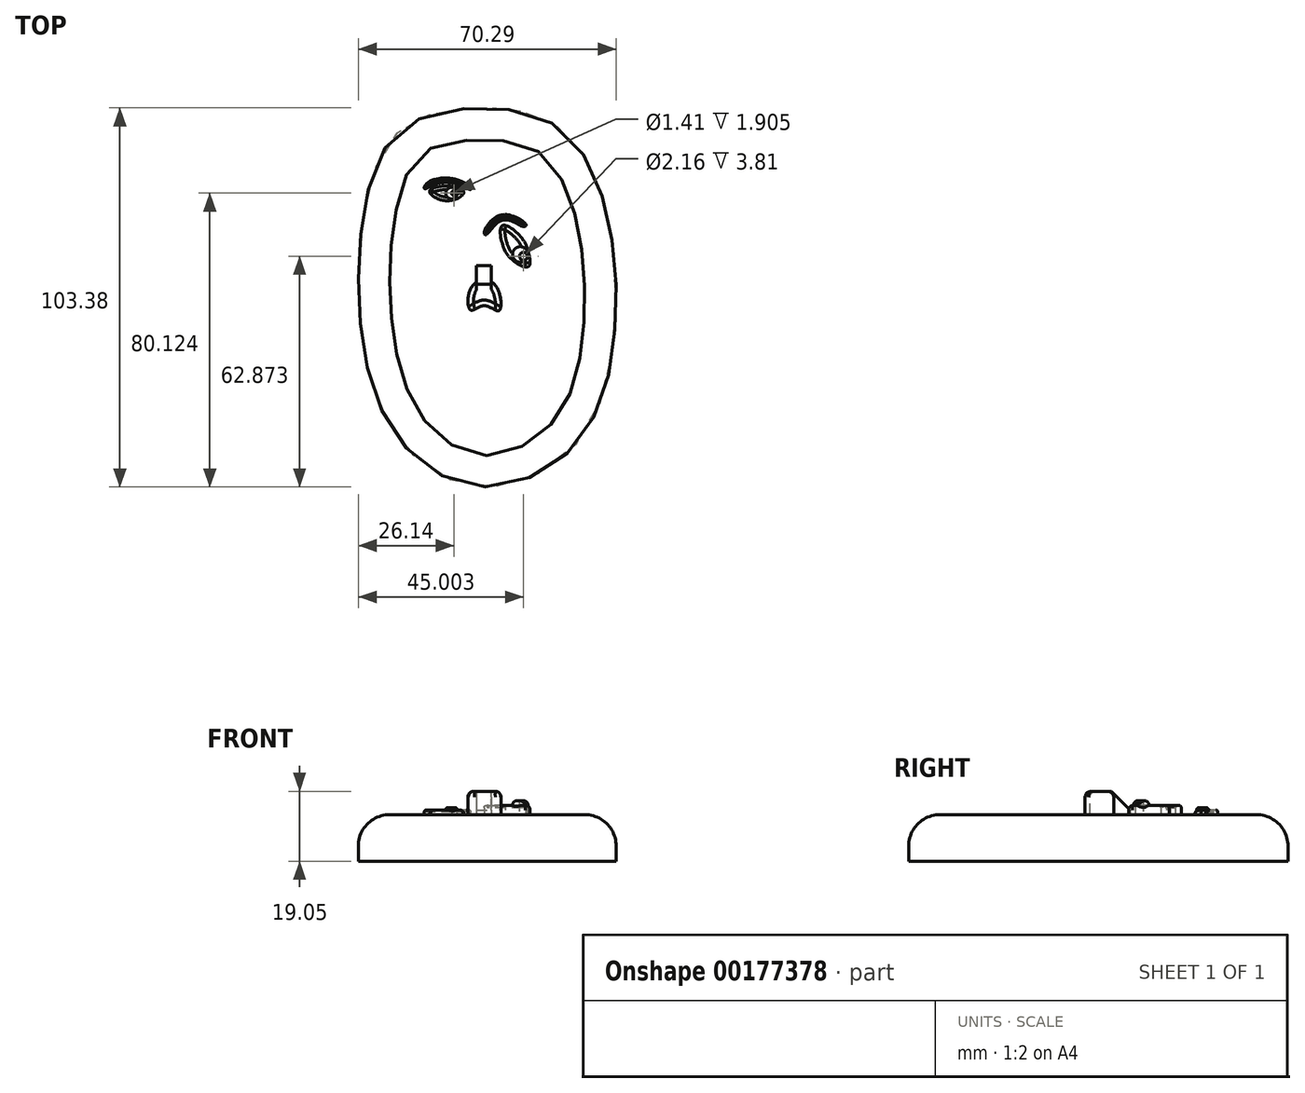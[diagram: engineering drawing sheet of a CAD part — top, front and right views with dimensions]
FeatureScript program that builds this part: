
annotation { "Feature Type Name" : "Feature", "Feature Type Description" : "" }
export const myFeature = defineFeature(function(context is Context, id is Id, definition is map)
    precondition{}
    {
        {
            var Q0;
            Q0=qCreatedBy(makeId("Top.planeOp"),FACE);
            var sketch = newSketch(context, id + "F0", { "sketchPlane" : qUnion([Q0])});
            skFitSpline(sketch, "E0", {"points": [v(-5.64, 49.3) * mm, v(-21.96, 44.26) * mm, v(-32.02, 25.34) * mm, v(-33.58, -10.93) * mm, v(-22.82, -41.3) * mm, v(0, -53.8) * mm, v(25.08, -42) * mm, v(35.5, -12.32) * mm, v(32.2, 25.34) * mm, v(19.53, 44.78) * mm, v(4.95, 49.3) * mm, v(-5.64, 49.3) * mm]});
            skSolve(sketch);
        }
        {
            var Q0;
            Q0=makeQuery(id+"F0.imprint","IMPRINT",FACE,{"disambiguationData":[TD([[makeQuery(id+"F0.imprint","IMPRINT",EDGE,{"derivedFrom":sQuery(id+"F0.wireOp",EDGE,"E0")}),1.0]])]});
            extrude(context, id + "F1", {"entities" : qUnion([Q0]), "depth" : 12.7 * mm});
        }
        {
            var Q0;
            Q0=makeQuery(id+"F1.opExtrude","CAP_EDGE",EDGE,{"disambiguationData":[OSD([sQuery(id+"F0.wireOp",EDGE,"E0")])],"isStart":false});
            fillet(context, id + "F2", {"entities" : qUnion([Q0]), "radius" : 8.58 * mm, "tangentPropagation" : true, "allowEdgeOverflow" : false});
        }
        {
            var Q0;
            Q0=makeQuery(id+"F1.opExtrude","CAP_FACE",FACE,{"disambiguationData":[OSD([sQuery(id+"F0.wireOp",EDGE,"E0")])],"isStart":false});
            var sketch = newSketch(context, id + "F3", { "sketchPlane" : qUnion([Q0])});
            skFitSpline(sketch, "E1", {"points": [v(-14.92, 26.83) * mm, v(-12.77, 28) * mm, v(-8.2, 28.03) * mm, v(-5.58, 26.54) * mm, v(-8.03, 24.57) * mm, v(-12.73, 24.79) * mm, v(-14.92, 26.83) * mm]});
            skCircle(sketch, "E2", {"center": v(-8.94, 26.28) * mm, "radius": 1.57 * mm});
            skCircle(sketch, "E3", {"center": v(-8.94, 26.28) * mm, "radius": 0.84 * mm});
            skSolve(sketch);
        }
        {
            var Q0;
            Q0=makeQuery(id+"F3.imprint","IMPRINT",FACE,{"disambiguationData":[TD([[makeQuery(id+"F3.imprint","IMPRINT",EDGE,{"derivedFrom":sQuery(id+"F3.wireOp",EDGE,"E1")}),-1.0]])]});
            extrude(context, id + "F4", {"entities" : qUnion([Q0]), "operationType" : NewBodyOperationType.ADD, "depth" : 1.27 * mm});
        }
        {
            var Q0;
            Q0=makeQuery(id+"F4.boolean.opBoolean","SPLIT",FACE,{"disambiguationData":[TD([makeQuery(id+"F4.opExtrude","SWEPT_FACE",FACE,{"disambiguationData":[OSD([sQuery(id+"F3.wireOp",EDGE,"E2")])]})])],"derivedFrom":makeQuery(id+"F1.opExtrude","CAP_FACE",FACE,{"disambiguationData":[OSD([sQuery(id+"F0.wireOp",EDGE,"E0")])],"isStart":false})});
            var sketch = newSketch(context, id + "F5", { "sketchPlane" : qUnion([Q0])});
            skCircle(sketch, "E4", {"center": v(-8.21, 26.31) * mm, "radius": 0.7 * mm});
            skCircle(sketch, "E5", {"center": v(-8.21, 26.31) * mm, "radius": 0.3 * mm});
            skSolve(sketch);
        }
        {
            var Q0;
            Q0=makeQuery(id+"F5.imprint","IMPRINT",FACE,{"disambiguationData":[TD([[makeQuery(id+"F5.imprint","IMPRINT",EDGE,{"derivedFrom":sQuery(id+"F5.wireOp",EDGE,"E4")}),-1.0]])]});
            extrude(context, id + "F6", {"entities" : qUnion([Q0]), "operationType" : NewBodyOperationType.ADD, "depth" : 1.9 * mm});
        }
        {
            var Q0;
            Q0=makeQuery(id+"F4.opExtrude","CAP_EDGE",EDGE,{"disambiguationData":[OSD([sQuery(id+"F3.wireOp",EDGE,"E1")])],"isStart":false});
            fillet(context, id + "F7", {"entities" : qUnion([Q0]), "radius" : 1.02 * mm, "tangentPropagation" : true, "allowEdgeOverflow" : false});
        }
        {
            var Q0;
            Q0=makeQuery(id+"F6.opExtrude","CAP_EDGE",EDGE,{"disambiguationData":[OSD([sQuery(id+"F3.wireOp",EDGE,"E2")])],"isStart":false});
            fillet(context, id + "F8", {"entities" : qUnion([Q0]), "radius" : 0.5 * mm, "tangentPropagation" : true, "allowEdgeOverflow" : false});
        }
        {
            var Q0;
            {var subQ0=sQuery(id+"F0.wireOp",EDGE,"E0");Q0=makeQuery(id+"F4.boolean.opBoolean","SPLIT",FACE,{"disambiguationData":[TD([makeQuery(id+"F2.opFillet","BLEND_FACE",FACE,{"disambiguationData":[OSD([subQ0])]})])],"derivedFrom":makeQuery(id+"F1.opExtrude","CAP_FACE",FACE,{"disambiguationData":[OSD([subQ0])],"isStart":false})});}
            var sketch = newSketch(context, id + "F9", { "sketchPlane" : qUnion([Q0])});
            skFitSpline(sketch, "E6", {"points": [v(-15.7, 27.64) * mm, v(-10.41, 29.23) * mm, v(-4.31, 27.4) * mm, v(-3.73, 27.32) * mm, v(-3.75, 27.86) * mm, v(-6.87, 29.75) * mm, v(-10.24, 30.4) * mm, v(-14.3, 29.81) * mm, v(-16.27, 28.14) * mm, v(-16.27, 27.47) * mm, v(-15.7, 27.64) * mm]});
            skSolve(sketch);
        }
        {
            var Q0;
            Q0=makeQuery(id+"F9.imprint","IMPRINT",FACE,{"disambiguationData":[TD([[makeQuery(id+"F9.imprint","IMPRINT",EDGE,{"derivedFrom":sQuery(id+"F9.wireOp",EDGE,"E6")}),1.0]])]});
            extrude(context, id + "F10", {"entities" : qUnion([Q0]), "operationType" : NewBodyOperationType.ADD, "depth" : 1.27 * mm});
        }
        {
            var Q0;
            Q0=makeQuery(id+"F10.opExtrude","CAP_EDGE",EDGE,{"disambiguationData":[OSD([sQuery(id+"F9.wireOp",EDGE,"E6")])],"isStart":false});
            fillet(context, id + "F11", {"entities" : qUnion([Q0]), "radius" : 0.5 * mm, "tangentPropagation" : true, "allowEdgeOverflow" : false});
        }
        {
            var Q0;
            {var subQ0=sQuery(id+"F0.wireOp",EDGE,"E0");Q0=makeQuery(id+"F4.boolean.opBoolean","SPLIT",FACE,{"disambiguationData":[TD([makeQuery(id+"F2.opFillet","BLEND_FACE",FACE,{"disambiguationData":[OSD([subQ0])]})])],"derivedFrom":makeQuery(id+"F1.opExtrude","CAP_FACE",FACE,{"disambiguationData":[OSD([subQ0])],"isStart":false})});}
            var sketch = newSketch(context, id + "F12", { "sketchPlane" : qUnion([Q0])});
            skFitSpline(sketch, "E7", {"points": [v(4.9, 17.42) * mm, v(9.33, 15.05) * mm, v(12.12, 9.89) * mm, v(12.01, 6.28) * mm, v(7.94, 7.82) * mm, v(4.92, 12.44) * mm, v(4.9, 17.42) * mm]});
            skCircle(sketch, "E8", {"center": v(9.8, 9.58) * mm, "radius": 2.12 * mm});
            skCircle(sketch, "E9", {"center": v(10.29, 8.73) * mm, "radius": 1.03 * mm});
            skSolve(sketch);
        }
        {
            var Q0;
            Q0=makeQuery(id+"F12.imprint","IMPRINT",FACE,{"disambiguationData":[TD([[makeQuery(id+"F12.imprint","IMPRINT",EDGE,{"derivedFrom":sQuery(id+"F12.wireOp",EDGE,"E7")}),-1.0]])]});
            extrude(context, id + "F13", {"entities" : qUnion([Q0]), "operationType" : NewBodyOperationType.ADD, "depth" : 2.54 * mm});
        }
        {
            var Q0;
            Q0=makeQuery(id+"F13.opExtrude","CAP_EDGE",EDGE,{"disambiguationData":[OSD([sQuery(id+"F12.wireOp",EDGE,"E7")])],"isStart":false});
            fillet(context, id + "F14", {"entities" : qUnion([Q0]), "radius" : 1.27 * mm, "tangentPropagation" : true, "allowEdgeOverflow" : false});
        }
        {
            var Q0;
            {var subQ0=sQuery(id+"F0.wireOp",EDGE,"E0");Q0=makeQuery(id+"F13.boolean.opBoolean","SPLIT",FACE,{"disambiguationData":[TD([makeQuery(id+"F13.opExtrude","SWEPT_FACE",FACE,{"disambiguationData":[OSD([sQuery(id+"F12.wireOp",EDGE,"E8")])]})])],"derivedFrom":makeQuery(id+"F4.boolean.opBoolean","SPLIT",FACE,{"disambiguationData":[TD([makeQuery(id+"F2.opFillet","BLEND_FACE",FACE,{"disambiguationData":[OSD([subQ0])]})])],"derivedFrom":makeQuery(id+"F1.opExtrude","CAP_FACE",FACE,{"disambiguationData":[OSD([subQ0])],"isStart":false})})});}
            var sketch = newSketch(context, id + "F15", { "sketchPlane" : qUnion([Q0])});
            skCircle(sketch, "E10", {"center": v(10.65, 9.06) * mm, "radius": 1.08 * mm});
            skSolve(sketch);
        }
        {
            var Q0;
            Q0=makeQuery(id+"F15.imprint","IMPRINT",FACE,{"disambiguationData":[TD([[makeQuery(id+"F15.imprint","IMPRINT",EDGE,{"derivedFrom":sQuery(id+"F15.wireOp",EDGE,"E10")}),-1.0]])]});
            extrude(context, id + "F16", {"entities" : qUnion([Q0]), "operationType" : NewBodyOperationType.ADD, "depth" : 3.8 * mm});
        }
        {
            var Q0;
            Q0=makeQuery(id+"F16.opExtrude","CAP_EDGE",EDGE,{"disambiguationData":[OSD([sQuery(id+"F12.wireOp",EDGE,"E8")])],"isStart":false});
            fillet(context, id + "F17", {"entities" : qUnion([Q0]), "radius" : 1.27 * mm, "tangentPropagation" : true, "allowEdgeOverflow" : false});
        }
        {
            var Q0;
            {var subQ0=sQuery(id+"F0.wireOp",EDGE,"E0");var subQ1=makeQuery(id+"F2.opFillet","BLEND_FACE",FACE,{"disambiguationData":[OSD([subQ0])]});Q0=makeQuery(id+"F13.boolean.opBoolean","SPLIT",FACE,{"disambiguationData":[TD([subQ1])],"derivedFrom":makeQuery(id+"F4.boolean.opBoolean","SPLIT",FACE,{"disambiguationData":[TD([subQ1])],"derivedFrom":makeQuery(id+"F1.opExtrude","CAP_FACE",FACE,{"disambiguationData":[OSD([subQ0])],"isStart":false})})});}
            var sketch = newSketch(context, id + "F18", { "sketchPlane" : qUnion([Q0])});
            skFitSpline(sketch, "E11", {"points": [v(0.79, 15.18) * mm, v(5.22, 19) * mm, v(10.67, 17.17) * mm, v(11.31, 17.38) * mm, v(11.16, 18.05) * mm, v(4.68, 20.37) * mm, v(0, 15.75) * mm, v(0.2, 14.98) * mm, v(0.79, 15.18) * mm]});
            skSolve(sketch);
        }
        {
            var Q0;
            Q0=makeQuery(id+"F18.imprint","IMPRINT",FACE,{"disambiguationData":[TD([[makeQuery(id+"F18.imprint","IMPRINT",EDGE,{"derivedFrom":sQuery(id+"F18.wireOp",EDGE,"E11")}),1.0]])]});
            extrude(context, id + "F19", {"entities" : qUnion([Q0]), "operationType" : NewBodyOperationType.ADD, "depth" : 2.54 * mm});
        }
        {
            var Q0;
            Q0=makeQuery(id+"F19.opExtrude","CAP_EDGE",EDGE,{"disambiguationData":[OSD([sQuery(id+"F18.wireOp",EDGE,"E11")])],"isStart":false});
            fillet(context, id + "F20", {"entities" : qUnion([Q0]), "radius" : 0.64 * mm, "tangentPropagation" : true, "allowEdgeOverflow" : false});
        }
        {
            var Q0;
            {var subQ0=sQuery(id+"F0.wireOp",EDGE,"E0");var subQ1=makeQuery(id+"F2.opFillet","BLEND_FACE",FACE,{"disambiguationData":[OSD([subQ0])]});Q0=makeQuery(id+"F13.boolean.opBoolean","SPLIT",FACE,{"disambiguationData":[TD([subQ1])],"derivedFrom":makeQuery(id+"F4.boolean.opBoolean","SPLIT",FACE,{"disambiguationData":[TD([subQ1])],"derivedFrom":makeQuery(id+"F1.opExtrude","CAP_FACE",FACE,{"disambiguationData":[OSD([subQ0])],"isStart":false})})});}
            var sketch = newSketch(context, id + "F21", { "sketchPlane" : qUnion([Q0])});
            skLineSegment(sketch, "E12", {"start": v(-2.2, 6.58) * mm, "end": v(-2.2, -1.93) * mm});
            skLineSegment(sketch, "E13", {"start": v(-2.2, -1.93) * mm, "end": v(1.93, -1.93) * mm});
            skLineSegment(sketch, "E14", {"start": v(1.93, -1.93) * mm, "end": v(1.93, 6.6) * mm});
            skLineSegment(sketch, "E15", {"start": v(1.93, 6.6) * mm, "end": v(-2.2, 6.58) * mm});
            skFitSpline(sketch, "E16", {"points": [v(-2.2, 1.95) * mm, v(-4.43, -2.34) * mm, v(-3.58, -5.64) * mm, v(0, -4.38) * mm, v(3.9, -5.78) * mm, v(4.32, -1.94) * mm, v(1.93, 2.05) * mm, v(-2.2, 1.95) * mm]});
            skSolve(sketch);
        }
        {
            var Q0;
            {var subQ0=sQuery(id+"F21.wireOp",EDGE,"E15");Q0=makeQuery(id+"F21.imprint","IMPRINT",FACE,{"disambiguationData":[TD([[makeQuery(id+"F21.imprint","IMPRINT",EDGE,{"derivedFrom":subQ0}),1.0]])]});}
            var Q1;
            {var subQ0=sQuery(id+"F21.wireOp",EDGE,"E13");Q1=makeQuery(id+"F21.imprint","IMPRINT",FACE,{"disambiguationData":[TD([[makeQuery(id+"F21.imprint","IMPRINT",EDGE,{"derivedFrom":subQ0}),1.0]])]});}
            var Q2;
            {var subQ0=sQuery(id+"F21.wireOp",EDGE,"E13");Q2=makeQuery(id+"F21.imprint","IMPRINT",FACE,{"disambiguationData":[TD([[makeQuery(id+"F21.imprint","IMPRINT",EDGE,{"derivedFrom":subQ0}),-1.0]])]});}
            extrude(context, id + "F22", {"entities" : qUnion([Q0, Q1, Q2]), "operationType" : NewBodyOperationType.ADD, "depth" : 6.35 * mm});
        }
        {
            var Q0;
            Q0=makeQuery(id+"F22.opExtrude","CAP_EDGE",EDGE,{"disambiguationData":[OSD([sQuery(id+"F21.wireOp",EDGE,"E15")])],"isStart":false});
            chamfer(context, id + "F23", {"entities" : qUnion([Q0]), "width" : 5.08 * mm, "tangentPropagation" : true});
        }
        {
            var Q0;
            Q0=makeQuery(id+"F22.opExtrude","CAP_EDGE",EDGE,{"disambiguationData":[OSD([sQuery(id+"F21.wireOp",EDGE,"E16")])],"isStart":false});
            fillet(context, id + "F24", {"entities" : qUnion([Q0]), "radius" : 1.52 * mm, "tangentPropagation" : true, "allowEdgeOverflow" : false});
        }
    });
